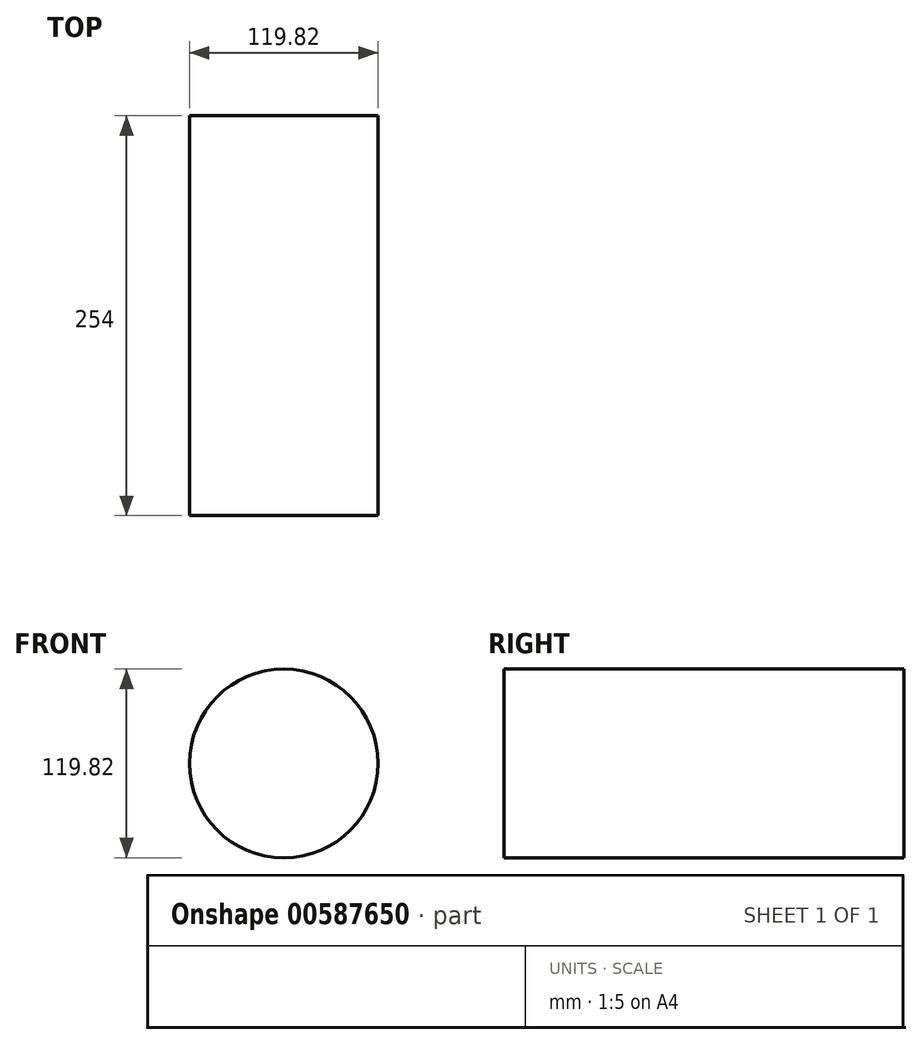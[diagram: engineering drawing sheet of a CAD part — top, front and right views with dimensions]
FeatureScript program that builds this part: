
annotation { "Feature Type Name" : "Feature", "Feature Type Description" : "" }
export const myFeature = defineFeature(function(context is Context, id is Id, definition is map)
    precondition{}
    {
        {
            var Q0;
            Q0=qCreatedBy(makeId("Front.planeOp"),FACE);
            var sketch = newSketch(context, id + "F0", { "sketchPlane" : qUnion([Q0])});
            skCircle(sketch, "E0", {"center": v(0, 0) * mm, "radius": 59.9 * mm});
            skSolve(sketch);
        }
        {
            var Q0;
            Q0 = qSketchRegion(id + "F0", true);
            extrude(context, id + "F1", {"entities" : qUnion([Q0]), "depth" : 254 * mm, "offsetDistance" : 25.4 * mm});
        }
    });
